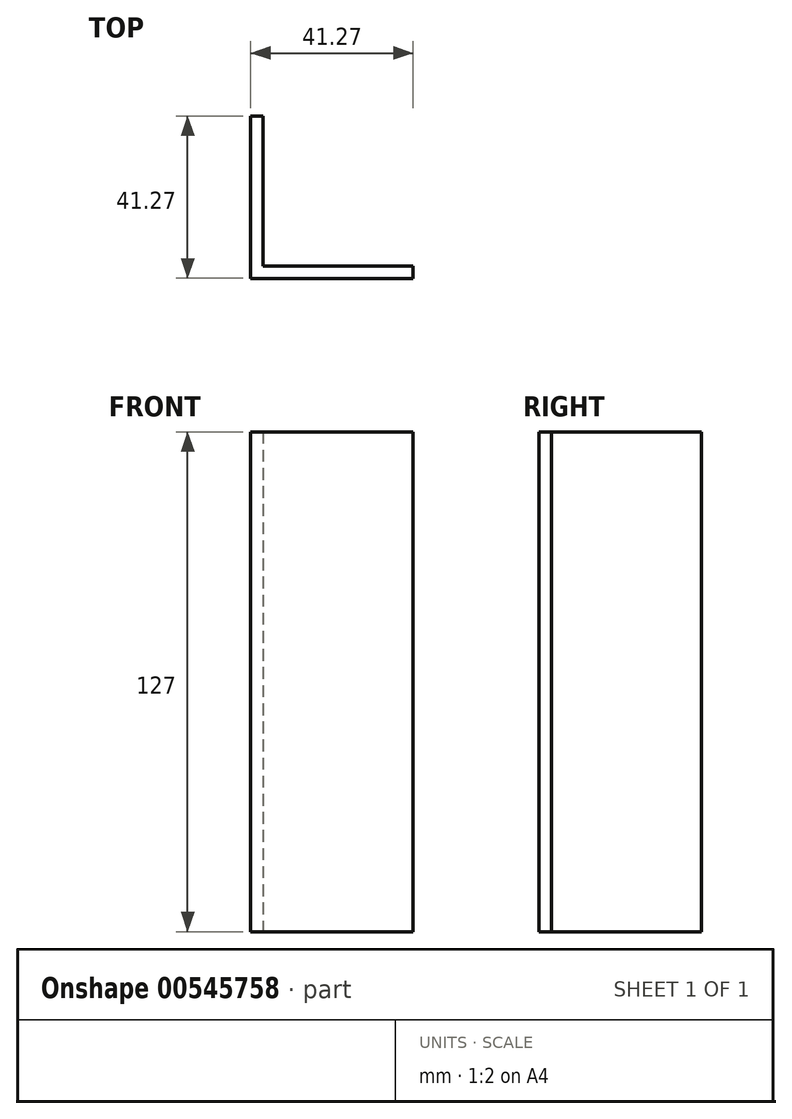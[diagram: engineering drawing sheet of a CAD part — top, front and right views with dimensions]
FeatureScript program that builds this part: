
annotation { "Feature Type Name" : "Feature", "Feature Type Description" : "" }
export const myFeature = defineFeature(function(context is Context, id is Id, definition is map)
    precondition{}
    {
        {
            var Q0;
            Q0=qCreatedBy(makeId("Front.planeOp"),FACE);
            var sketch = newSketch(context, id + "F0", { "sketchPlane" : qUnion([Q0])});
            skLineSegment(sketch, "E0.bottom", {"start": v(-32.68, -52.68) * mm, "end": v(34, -52.68) * mm});
            skLineSegment(sketch, "E0.top", {"start": v(-32.68, 74.32) * mm, "end": v(34, 74.32) * mm});
            skLineSegment(sketch, "E0.left", {"start": v(-32.68, -52.68) * mm, "end": v(-32.68, 74.32) * mm});
            skLineSegment(sketch, "E0.right", {"start": v(34, -52.68) * mm, "end": v(34, 74.32) * mm});
            skLineSegment(sketch, "E1", {"start": v(-32.68, 23.52) * mm, "end": v(34, 23.52) * mm});
            skLineSegment(sketch, "E2", {"start": v(-32.68, -8.23) * mm, "end": v(34, -8.23) * mm});
            skLineSegment(sketch, "E3", {"start": v(-4.1, 74.32) * mm, "end": v(-4.1, -52.68) * mm});
            skSolve(sketch);
        }
        {
            var Q0;
            {var subQ0=sQuery(id+"F0.wireOp",EDGE,"E1");var subQ1=sQuery(id+"F0.wireOp",EDGE,"E0.left");var subQ2=makeQuery(id+"F0.imprint","INTERSECT",VERTEX,{"derivedFrom":[subQ1,subQ0]});Q0=makeQuery(id+"F0.imprint","IMPRINT",FACE,{"disambiguationData":[TD([[makeQuery(id+"F0.imprint","IMPRINT",EDGE,{"disambiguationData":[TD([[subQ2,1.0]])],"derivedFrom":subQ1}),-1.0]])]});}
            extrude(context, id + "F1", {"entities" : qUnion([Q0]), "depth" : 1.59 * mm, "offsetDistance" : 25.4 * mm});
        }
        {
            var Q0;
            Q0=makeQuery(id+"F1.opExtrude","SWEPT_FACE",FACE,{"disambiguationData":[OSD([sQuery(id+"F0.wireOp",EDGE,"E3")])]});
            var sketch = newSketch(context, id + "F2", { "sketchPlane" : qUnion([Q0])});
            skLineSegment(sketch, "E4.bottom", {"start": v(0, -52.68) * mm, "end": v(-38.1, -52.68) * mm});
            skLineSegment(sketch, "E4.top", {"start": v(0, 74.32) * mm, "end": v(-38.1, 74.32) * mm});
            skLineSegment(sketch, "E4.left", {"start": v(0, -52.68) * mm, "end": v(0, 74.32) * mm});
            skLineSegment(sketch, "E4.right", {"start": v(-38.1, -52.68) * mm, "end": v(-38.1, 74.32) * mm});
            skSolve(sketch);
        }
        {
            var Q0;
            {var subQ5=sQuery(id+"F2.wireOp",EDGE,"E4.bottom");Q0=makeQuery(id+"F2.imprint","IMPRINT",FACE,{"disambiguationData":[TD([[makeQuery(id+"F2.imprint","IMPRINT",EDGE,{"derivedFrom":subQ5}),-1.0]])]});}
            extrude(context, id + "F3", {"entities" : qUnion([Q0]), "operationType" : NewBodyOperationType.ADD, "oppositeDirection" : true, "depth" : 3.17 * mm, "offsetDistance" : 25.4 * mm});
        }
        {
            var Q0;
            Q0=makeQuery(id+"F3.opExtrude","SWEPT_FACE",FACE,{"disambiguationData":[OSD([sQuery(id+"F2.wireOp",EDGE,"E4.right")])]});
            var sketch = newSketch(context, id + "F4", { "sketchPlane" : qUnion([Q0])});
            skLineSegment(sketch, "E5.bottom", {"start": v(-7.28, -52.68) * mm, "end": v(34, -52.68) * mm});
            skLineSegment(sketch, "E5.top", {"start": v(-7.28, 74.32) * mm, "end": v(34, 74.32) * mm});
            skLineSegment(sketch, "E5.left", {"start": v(-7.28, -52.68) * mm, "end": v(-7.28, 74.32) * mm});
            skLineSegment(sketch, "E5.right", {"start": v(34, -52.68) * mm, "end": v(34, 74.32) * mm});
            skSolve(sketch);
        }
        {
            var Q0;
            {var subQ2=sQuery(id+"F4.wireOp",EDGE,"E5.right");Q0=makeQuery(id+"F4.imprint","IMPRINT",FACE,{"disambiguationData":[TD([[makeQuery(id+"F4.imprint","IMPRINT",EDGE,{"derivedFrom":subQ2}),1.0]])]});}
            var Q1;
            {var subQ2=sQuery(id+"F4.wireOp",EDGE,"E5.left");Q1=makeQuery(id+"F4.imprint","IMPRINT",FACE,{"disambiguationData":[TD([[makeQuery(id+"F4.imprint","IMPRINT",EDGE,{"derivedFrom":subQ2}),-1.0]])]});}
            extrude(context, id + "F5", {"entities" : qUnion([Q0, Q1]), "operationType" : NewBodyOperationType.ADD, "depth" : 3.17 * mm, "offsetDistance" : 25.4 * mm});
        }
        {
            var Q0;
            Q0=makeQuery(id+"F1.opExtrude","CAP_FACE",FACE,{"disambiguationData":[OSD([sQuery(id+"F0.wireOp",EDGE,"E0.left"),sQuery(id+"F0.wireOp",EDGE,"E1"),sQuery(id+"F0.wireOp",EDGE,"E2"),sQuery(id+"F0.wireOp",EDGE,"E3")])],"isStart":false});
            var sketch = newSketch(context, id + "F6", { "sketchPlane" : qUnion([Q0])});
            skCircle(sketch, "E6", {"center": v(-16.68, 7.64) * mm, "radius": 4 * mm});
            skLineSegment(sketch, "E7", {"start": v(-16.68, -0.36) * mm, "end": v(-16.68, 15.64) * mm, "construction": true});
            skLineSegment(sketch, "E8", {"start": v(-8.68, 7.64) * mm, "end": v(-24.68, 7.64) * mm, "construction": true});
            skLineSegment(sketch, "E9", {"start": v(-22.34, 13.3) * mm, "end": v(-11.03, 1.99) * mm, "construction": true});
            skLineSegment(sketch, "E10", {"start": v(-22.34, 1.99) * mm, "end": v(-11.03, 13.3) * mm, "construction": true});
            skCircle(sketch, "E11", {"center": v(-22.34, 13.3) * mm, "radius": 1.85 * mm});
            skCircle(sketch, "E12", {"center": v(-16.68, 15.64) * mm, "radius": 1.85 * mm});
            skCircle(sketch, "E13", {"center": v(-11.03, 13.3) * mm, "radius": 1.85 * mm});
            skCircle(sketch, "E14", {"center": v(-24.68, 7.64) * mm, "radius": 1.85 * mm});
            skCircle(sketch, "E15", {"center": v(-8.68, 7.64) * mm, "radius": 1.85 * mm});
            skCircle(sketch, "E16", {"center": v(-16.68, -0.36) * mm, "radius": 1.85 * mm});
            skCircle(sketch, "E17", {"center": v(-11.03, 1.99) * mm, "radius": 1.85 * mm});
            skCircle(sketch, "E18", {"center": v(-22.34, 1.99) * mm, "radius": 1.85 * mm});
            skLineSegment(sketch, "E19", {"start": v(-32.68, 23.52) * mm, "end": v(-32.68, -8.23) * mm});
            skSolve(sketch);
        }
        {
            var Q0;
            Q0=makeQuery(id+"F6.imprint","IMPRINT",FACE,{"disambiguationData":[TD([[makeQuery(id+"F6.imprint","IMPRINT",EDGE,{"derivedFrom":sQuery(id+"F6.wireOp",EDGE,"E6")}),1.0]])]});
            var Q1;
            Q1=makeQuery(id+"F6.imprint","IMPRINT",FACE,{"disambiguationData":[TD([[makeQuery(id+"F6.imprint","IMPRINT",EDGE,{"derivedFrom":sQuery(id+"F6.wireOp",EDGE,"E11")}),1.0]])]});
            var Q2;
            Q2=makeQuery(id+"F6.imprint","IMPRINT",FACE,{"disambiguationData":[TD([[makeQuery(id+"F6.imprint","IMPRINT",EDGE,{"derivedFrom":sQuery(id+"F6.wireOp",EDGE,"E12")}),1.0]])]});
            var Q3;
            Q3=makeQuery(id+"F6.imprint","IMPRINT",FACE,{"disambiguationData":[TD([[makeQuery(id+"F6.imprint","IMPRINT",EDGE,{"derivedFrom":sQuery(id+"F6.wireOp",EDGE,"E13")}),1.0]])]});
            var Q4;
            Q4=makeQuery(id+"F6.imprint","IMPRINT",FACE,{"disambiguationData":[TD([[makeQuery(id+"F6.imprint","IMPRINT",EDGE,{"derivedFrom":sQuery(id+"F6.wireOp",EDGE,"E17")}),1.0]])]});
            var Q5;
            Q5=makeQuery(id+"F6.imprint","IMPRINT",FACE,{"disambiguationData":[TD([[makeQuery(id+"F6.imprint","IMPRINT",EDGE,{"derivedFrom":sQuery(id+"F6.wireOp",EDGE,"E16")}),1.0]])]});
            var Q6;
            Q6=makeQuery(id+"F6.imprint","IMPRINT",FACE,{"disambiguationData":[TD([[makeQuery(id+"F6.imprint","IMPRINT",EDGE,{"derivedFrom":sQuery(id+"F6.wireOp",EDGE,"E18")}),1.0]])]});
            var Q7;
            Q7=makeQuery(id+"F6.imprint","IMPRINT",FACE,{"disambiguationData":[TD([[makeQuery(id+"F6.imprint","IMPRINT",EDGE,{"derivedFrom":sQuery(id+"F6.wireOp",EDGE,"E14")}),1.0]])]});
            extrude(context, id + "F7", {"entities" : qUnion([Q0, Q1, Q2, Q3, Q4, Q5, Q6, Q7]), "operationType" : NewBodyOperationType.REMOVE, "oppositeDirection" : true, "depth" : 25.4 * mm, "offsetDistance" : 25.4 * mm});
        }
        {
            var Q0;
            Q0=makeQuery(id+"F1.opExtrude","SWEPT_FACE",FACE,{"disambiguationData":[OSD([sQuery(id+"F0.wireOp",EDGE,"E0.left")])]});
            var sketch = newSketch(context, id + "F8", { "sketchPlane" : qUnion([Q0])});
            skLineSegment(sketch, "E20.bottom", {"start": v(0, -8.23) * mm, "end": v(1.59, -8.23) * mm});
            skLineSegment(sketch, "E20.top", {"start": v(0, 23.52) * mm, "end": v(1.59, 23.52) * mm});
            skLineSegment(sketch, "E20.left", {"start": v(0, -8.23) * mm, "end": v(0, 23.52) * mm});
            skLineSegment(sketch, "E20.right", {"start": v(1.59, -8.23) * mm, "end": v(1.59, 23.52) * mm});
            skSolve(sketch);
        }
        {
            var Q0;
            Q0=makeQuery(id+"F8.imprint","IMPRINT",FACE,{"disambiguationData":[TD([[makeQuery(id+"F8.imprint","IMPRINT",EDGE,{"derivedFrom":sQuery(id+"F8.wireOp",EDGE,"E20.bottom")}),-1.0]])]});
            extrude(context, id + "F9", {"entities" : qUnion([Q0]), "operationType" : NewBodyOperationType.REMOVE, "oppositeDirection" : true, "depth" : 25.4 * mm, "offsetDistance" : 25.4 * mm});
        }
    });
